# Revit family: IS_ConnectAir_A7015_BIM_IT
name_source: partatom
category: Plumbing Fixtures
revit_build: Autodesk Revit 2017 (Build: 20160225_1515(x64)
units: mm (PartAtom-declared; Revit-internal decimal feet)

## family parameters
Always vertical = No
Cut with Voids When Loaded = No
OmniClass Number = 23.45.55.17
OmniClass Title = Mixing Faucets
Part Type = Normal
Room Calculation Point = No
Round Connector Dimension = Use Diameter
Shared = No
Work Plane-Based = No

## types (1)
- A7015AA - C.AIR MISC.MC LAVABO  GR 5L/M S/PIL
    Accessori = http://www.idealstandard.it
    AltezzaNominale = 170 mm  [stored 0.557743 ft]
    Autore = Ideal Standard
    BIMobject main category = Sanitary
    BIMobject main category code = sanitary
    BOSUseNativeGeometries = 1
    Brand url = http://www.idealstandard.co.uk
    Caratteristiche = C.AIR MISC.MC LAVABO  GR 5L/M S/PIL
    CodiceABarre = 4015413342032
    CodiceDiPrestazione = EN
    Colore = cromo
    Connessione = piombatura
    Cost = 0 $
    CostoDiSostituzione = 0 $
    Date of publishing = 2018_04_19
    Description = C.AIR MISC.MC LAVABO  GR 5L/M S/PIL
    DescrizioneClassifcazioneUni2015 = IfcSanitaryTerminalType
    Dimensione = 48 x 162 x 170 mm
    EAN code = https://4015413342032
    Edition number = 1
    Finitura = cromo
    Forma = scolpito
    Garanzia = garanzia del produttore
    IFC Classification = Sanitary Terminal
    IfcEsportaCome = IfcSanitaryTerminalType
    InformazioniDiProdotto = http://www.idealstandard.it
    Installation instructions = http://www.idealstandard.it
    InstruzioniInstallazione = http://www.idealstandard.it
    LarghezzaNominale = 48 mm  [stored 0.15748 ft]
    LunghezzaNominale = 162 mm  [stored 0.531496 ft]
    Manufacturer name = Ideal Standard
    Material main = Brassware
    Materiale = brassware
    Model = A7015AA
    ModelloDiRiferimento = C.AIR MISC.MC LAVABO  GR 5L/M S/PIL
    NBS Reference Code = 45-35-70/
    NBS Reference Description = Wash Basin And Trough Water Supply Fittings
    Nome = ISI_IdealStandard_BasinMixers_ConnectAir_A7015AA
    NomeOggettoBim = ISI_IdealStandard_BasinMixers_ConnectAir_A7015AA
    Nominal height = 170
    Nominal width = 48
    NominalHeight = 170 mm  [stored 0.557743 ft]
    NominalLength = 162 mm  [stored 0.531496 ft]
    NominalWidth = 48 mm  [stored 0.15748 ft]
    NumeroDiModello = A7015AA
    OmniClass Code = 23-31 11 00
    OmniClass Description = Faucets
    PartiDiRicambio = http://www.idealstandard.it
    PesoNetto = 1.88 Kg
    Product Guid = 30ff070c-d73d-44f8-b531-4f1d5881c7a6
    Product SKU = A7015
    Product certification = http://www.idealstandard.it
    Product data url = https://bimobject.com
    Product family = Sanitary
    Product group = BASIN MIXER
    Product name = C.AIR MISC.MC LAVABO  GR 5L/M S/PIL
    Product url = http://www.idealstandard.it
    ProfonditàNominale = 162 mm  [stored 0.531496 ft]
    QR code = http://bimobject.com
    Revisione = 1
    Riferimento = Pr_40_20_87_98
    RiferimentoClassificazioneUni2015 = Washbasin taps
    Size = 48 x 162 x 170 mm
    Sostenibilità = riciclabile
    Spazio = interno
    Technical description = http://www.idealstandard.it
    Telefono = 800 652 290
    TipoDiDato = Fisso
    TipoEspotazioneIfc = BASIN MIXER
    TipologiaVaso = Altro
    URL = http://www.idealstandard.it
    Uniclass 2.0 Code = Pr_40_20_87_98
    Uniclass 2.0 Description = Washbasin taps
    Uniclass 2015 Code = Pr_40_20_87_98
    Uniclass 2015 Name = Washbasin taps
    UnitàDurata = anno
    UnitàDurataGaranzia = anno
    UnitàLineare = millimetro
    UnitàMonetaria = €
    UnitàSuperficie = millimetro
    UnitàVolume = litro
    Versione = 1
    VersioneClassificazioneUni2015 = Products v1.1
    Weight Net (Kg) = 1.88

note: [stored X ft] marks values corroborated as IEEE doubles in the binary element streams (Revit-internal decimal feet)

## geometry (parser evidence)
native form markers: Sweep x2
no freeform markers — native parametric forms only
